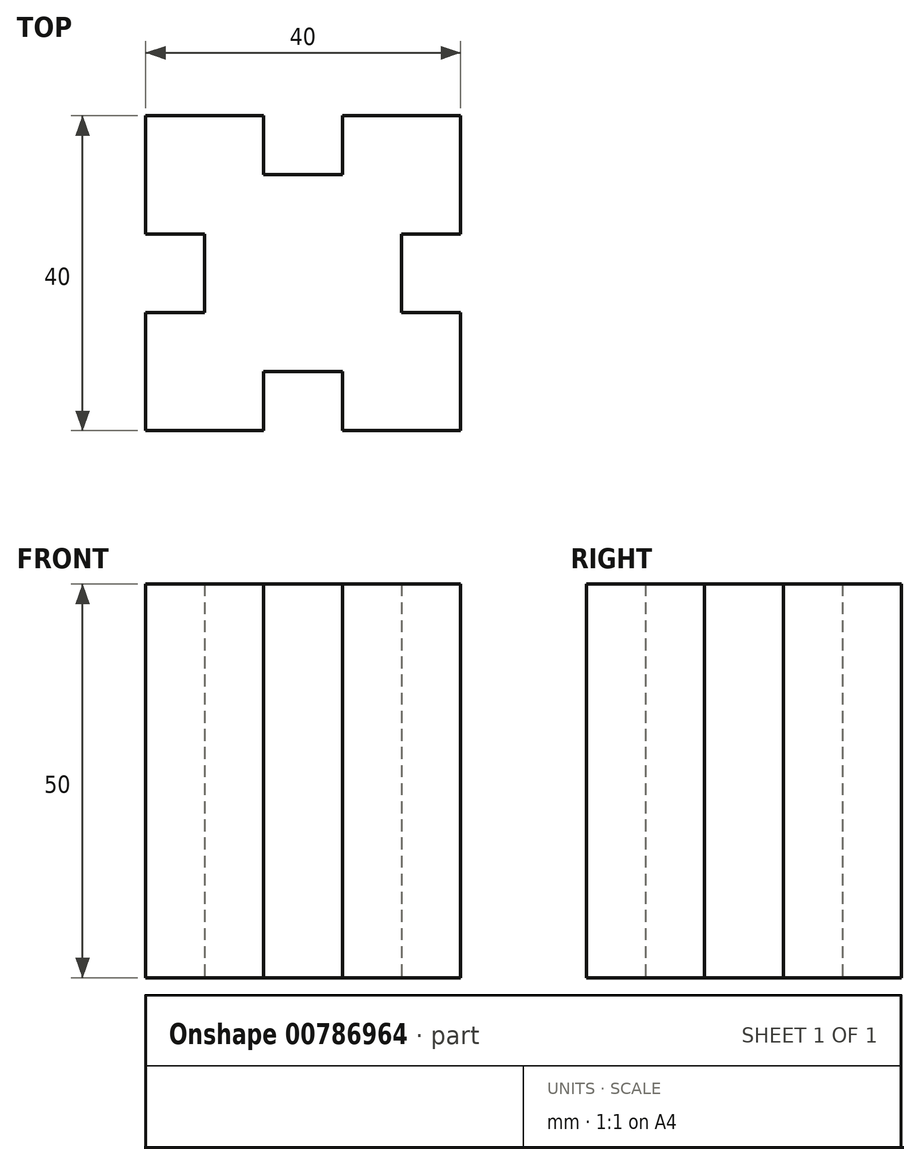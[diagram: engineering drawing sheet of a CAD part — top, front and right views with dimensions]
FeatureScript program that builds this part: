
annotation { "Feature Type Name" : "Feature", "Feature Type Description" : "" }
export const myFeature = defineFeature(function(context is Context, id is Id, definition is map)
    precondition{}
    {
        {
            var Q0;
            Q0=qCreatedBy(makeId("Top.planeOp"),FACE);
            var sketch = newSketch(context, id + "F0", { "sketchPlane" : qUnion([Q0])});
            skLineSegment(sketch, "E0.bottom", {"start": v(12.5, 12.5) * mm, "end": v(-12.5, 12.5) * mm});
            skLineSegment(sketch, "E0.top", {"start": v(12.5, -12.5) * mm, "end": v(-12.5, -12.5) * mm});
            skLineSegment(sketch, "E0.left", {"start": v(12.5, 12.5) * mm, "end": v(12.5, -12.5) * mm});
            skLineSegment(sketch, "E0.right", {"start": v(-12.5, 12.5) * mm, "end": v(-12.5, -12.5) * mm});
            skPoint(sketch, "E0.middle", {"position": v(0, 0) * mm});
            skLineSegment(sketch, "E1.bottom", {"start": v(20, 20) * mm, "end": v(5, 20) * mm});
            skLineSegment(sketch, "E1.top", {"start": v(20, 5) * mm, "end": v(5, 5) * mm});
            skLineSegment(sketch, "E1.left", {"start": v(20, 20) * mm, "end": v(20, 5) * mm});
            skLineSegment(sketch, "E1.right", {"start": v(5, 20) * mm, "end": v(5, 5) * mm});
            skPoint(sketch, "E1.middle", {"position": v(12.5, 12.5) * mm});
            skLineSegment(sketch, "E2.bottom", {"start": v(-5, 20) * mm, "end": v(-20, 20) * mm});
            skLineSegment(sketch, "E2.top", {"start": v(-5, 5) * mm, "end": v(-20, 5) * mm});
            skLineSegment(sketch, "E2.left", {"start": v(-5, 20) * mm, "end": v(-5, 5) * mm});
            skLineSegment(sketch, "E2.right", {"start": v(-20, 20) * mm, "end": v(-20, 5) * mm});
            skPoint(sketch, "E2.middle", {"position": v(-12.5, 12.5) * mm});
            skPoint(sketch, "E3.middle", {"position": v(-12.5, -12.5) * mm});
            skPoint(sketch, "E4.middle", {"position": v(12.5, -12.5) * mm});
            skLineSegment(sketch, "E5.bottom", {"start": v(20, -5) * mm, "end": v(5, -5) * mm});
            skLineSegment(sketch, "E5.top", {"start": v(20, -20) * mm, "end": v(5, -20) * mm});
            skLineSegment(sketch, "E5.left", {"start": v(20, -5) * mm, "end": v(20, -20) * mm});
            skLineSegment(sketch, "E5.right", {"start": v(5, -5) * mm, "end": v(5, -20) * mm});
            skLineSegment(sketch, "E6.bottom", {"start": v(-5, -5) * mm, "end": v(-20, -5) * mm});
            skLineSegment(sketch, "E6.top", {"start": v(-5, -20) * mm, "end": v(-20, -20) * mm});
            skLineSegment(sketch, "E6.left", {"start": v(-5, -5) * mm, "end": v(-5, -20) * mm});
            skLineSegment(sketch, "E6.right", {"start": v(-20, -5) * mm, "end": v(-20, -20) * mm});
            skSolve(sketch);
        }
        {
            var Q0;
            Q0 = qSketchRegion(id + "F0", true);
            extrude(context, id + "F1", {"entities" : qUnion([Q0]), "depth" : 50 * mm, "offsetDistance" : 25 * mm});
        }
    });
